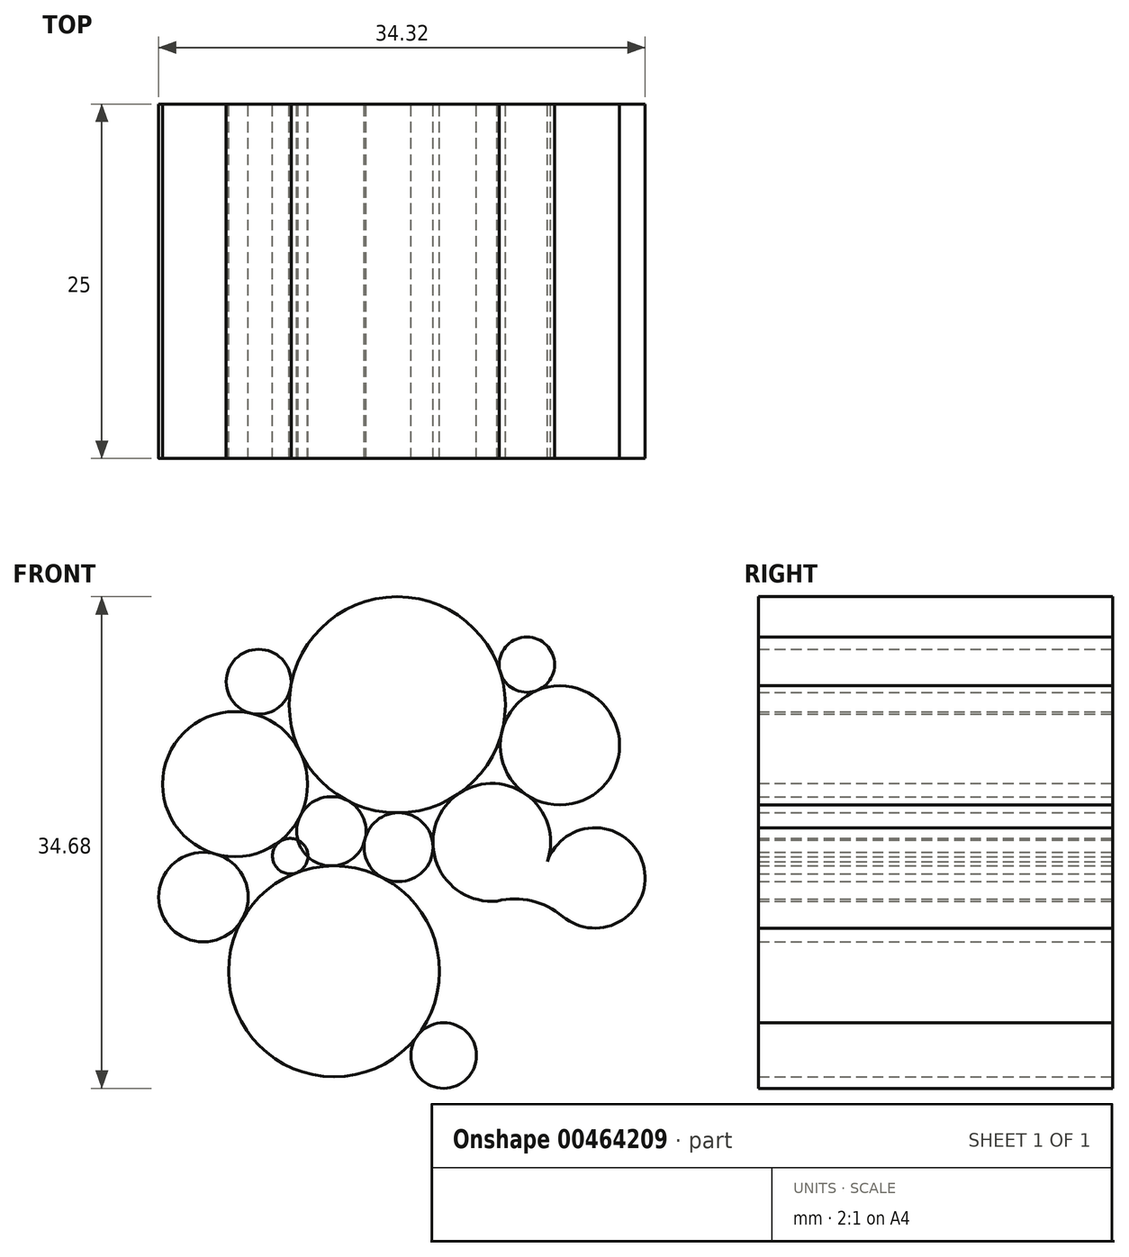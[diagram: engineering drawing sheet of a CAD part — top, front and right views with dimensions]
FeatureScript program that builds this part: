
annotation { "Feature Type Name" : "Feature", "Feature Type Description" : "" }
export const myFeature = defineFeature(function(context is Context, id is Id, definition is map)
    precondition{}
    {
        {
            var Q0;
            Q0=qCreatedBy(makeId("Front.planeOp"),FACE);
            var sketch = newSketch(context, id + "F0", { "sketchPlane" : qUnion([Q0])});
            skCircle(sketch, "E0", {"center": v(-5.15, 5.5) * mm, "radius": 17.5 * mm});
            skCircle(sketch, "E1", {"center": v(-5.33, 15.38) * mm, "radius": 7.62 * mm});
            skPoint(sketch, "E1.first.point", {"position": v(-5.47, 23) * mm});
            skPoint(sketch, "E1.second.point", {"position": v(-5.47, 23) * mm});
            skPoint(sketch, "E1.third.point", {"position": v(-3.02, 8.12) * mm});
            skCircle(sketch, "E2", {"center": v(6.14, 12.5) * mm, "radius": 4.2 * mm});
            skPoint(sketch, "E2.first.point", {"position": v(2.06, 13.53) * mm});
            skPoint(sketch, "E2.second.point", {"position": v(9.72, 14.73) * mm});
            skPoint(sketch, "E2.third.point", {"position": v(9.54, 10.03) * mm});
            skCircle(sketch, "E3", {"center": v(-16.77, 9.78) * mm, "radius": 5.12 * mm});
            skPoint(sketch, "E3.first.point", {"position": v(-12.18, 12.03) * mm});
            skPoint(sketch, "E3.second.point", {"position": v(-21.57, 11.55) * mm});
            skPoint(sketch, "E3.third.point", {"position": v(-16.32, 4.68) * mm});
            skCircle(sketch, "E4", {"center": v(3.81, 18.2) * mm, "radius": 1.95 * mm});
            skPoint(sketch, "E4.first.point", {"position": v(1.95, 17.63) * mm});
            skPoint(sketch, "E4.second.point", {"position": v(4.94, 19.8) * mm});
            skPoint(sketch, "E4.third.point", {"position": v(4.55, 16.4) * mm});
            skCircle(sketch, "E5", {"center": v(-9.98, 6.45) * mm, "radius": 2.44 * mm});
            skPoint(sketch, "E5.first.point", {"position": v(-12.18, 7.53) * mm});
            skPoint(sketch, "E5.second.point", {"position": v(-8.85, 8.62) * mm});
            skPoint(sketch, "E5.third.point", {"position": v(-8.97, 4.23) * mm});
            skCircle(sketch, "E6", {"center": v(1.34, 5.67) * mm, "radius": 4.16 * mm});
            skPoint(sketch, "E6.first.point", {"position": v(-1.02, 9.1) * mm});
            skPoint(sketch, "E6.second.point", {"position": v(4.58, 8.27) * mm});
            skPoint(sketch, "E6.third.point", {"position": v(-1.42, 2.56) * mm});
            skCircle(sketch, "E7", {"center": v(-15.1, 17) * mm, "radius": 2.3 * mm});
            skPoint(sketch, "E7.first.point", {"position": v(-16.6, 18.73) * mm});
            skPoint(sketch, "E7.second.point", {"position": v(-15.62, 14.77) * mm});
            skPoint(sketch, "E7.third.point", {"position": v(-12.85, 16.62) * mm});
            skLineSegment(sketch, "E8", {"start": v(3.81, 18.2) * mm, "end": v(1.95, 17.63) * mm, "construction": true});
            skCircle(sketch, "E9", {"center": v(-5.24, 5.33) * mm, "radius": 2.43 * mm});
            skPoint(sketch, "E9.first.point", {"position": v(-7.6, 5.89) * mm});
            skPoint(sketch, "E9.second.point", {"position": v(-5.26, 7.76) * mm});
            skPoint(sketch, "E9.third.point", {"position": v(-3.8, 3.37) * mm});
            skCircle(sketch, "E10", {"center": v(2.94, -3.62) * mm, "radius": 5.3 * mm});
            skPoint(sketch, "E10.first.point", {"position": v(1.71, 1.53) * mm});
            skPoint(sketch, "E10.second.point", {"position": v(-0.07, -7.99) * mm});
            skPoint(sketch, "E10.third.point", {"position": v(2.61, -8.91) * mm});
            skCircle(sketch, "E11", {"center": v(-19, 1.8) * mm, "radius": 3.16 * mm, "construction": true});
            skPoint(sketch, "E11.first.point", {"position": v(-16.28, 0.22) * mm});
            skPoint(sketch, "E11.second.point", {"position": v(-18.15, 4.85) * mm});
            skPoint(sketch, "E11.third.point", {"position": v(-22.06, 1) * mm});
            skCircle(sketch, "E12", {"center": v(-9.8, -3.43) * mm, "radius": 7.44 * mm});
            skPoint(sketch, "E12.first.point", {"position": v(-13.22, -10.03) * mm});
            skPoint(sketch, "E12.second.point", {"position": v(-9.94, 4.01) * mm});
            skPoint(sketch, "E12.third.point", {"position": v(-3.22, -6.9) * mm});
            skPoint(sketch, "E13.first.point", {"position": v(10.78, -1.74) * mm});
            skPoint(sketch, "E13.second.point", {"position": v(9.3, -1.63) * mm});
            skPoint(sketch, "E13.third.point", {"position": v(3.9, -4.41) * mm});
            skPoint(sketch, "E14.first.point", {"position": v(-3.5, -7.39) * mm});
            skPoint(sketch, "E14.third.point", {"position": v(-1.17, -6.97) * mm});
            skCircle(sketch, "E15", {"center": v(-19, 1.8) * mm, "radius": 3.16 * mm});
            skPoint(sketch, "E15.second.point", {"position": v(-15.89, 1.32) * mm});
            skPoint(sketch, "E15.third.point", {"position": v(-21.57, -0.04) * mm});
            skCircle(sketch, "E16", {"center": v(-12.88, 4.7) * mm, "radius": 1.25 * mm});
            skPoint(sketch, "E16.first.point", {"position": v(-13.53, 5.77) * mm});
            skPoint(sketch, "E16.second.point", {"position": v(-12.44, 3.53) * mm});
            skPoint(sketch, "E16.third.point", {"position": v(-11.74, 5.2) * mm});
            skCircle(sketch, "E17", {"center": v(8.61, 3.16) * mm, "radius": 3.54 * mm});
            skPoint(sketch, "E17.first.point", {"position": v(5.3, 1.9) * mm});
            skPoint(sketch, "E17.second.point", {"position": v(9.4, 6.61) * mm});
            skPoint(sketch, "E17.third.point", {"position": v(11.4, 5.33) * mm});
            skPoint(sketch, "E18.first.point", {"position": v(8.43, 5.29) * mm});
            skPoint(sketch, "E18.second.point", {"position": v(2.65, 1) * mm});
            skPoint(sketch, "E18.third.point", {"position": v(10.5, 1) * mm});
            skPoint(sketch, "E19.first.point", {"position": v(-0.71, -8.32) * mm});
            skPoint(sketch, "E19.second.point", {"position": v(3.23, -11.3) * mm});
            skPoint(sketch, "E19.third.point", {"position": v(-5.91, -11.98) * mm});
            skCircle(sketch, "E20", {"center": v(-2.06, -9.37) * mm, "radius": 2.31 * mm});
            skPoint(sketch, "E20.first.point", {"position": v(-4.3, -8.78) * mm});
            skPoint(sketch, "E20.second.point", {"position": v(0.07, -10.29) * mm});
            skPoint(sketch, "E20.third.point", {"position": v(-0.35, -10.93) * mm});
            skPoint(sketch, "E21.first.point", {"position": v(-0.43, -5.07) * mm});
            skPoint(sketch, "E21.second.point", {"position": v(3.23, -5.71) * mm});
            skPoint(sketch, "E22.first.point", {"position": v(15.25, 1.23) * mm});
            skPoint(sketch, "E22.second.point", {"position": v(11.56, -2.12) * mm});
            skPoint(sketch, "E22.third.point", {"position": v(14.07, 1.78) * mm});
            skPoint(sketch, "E23.first.point", {"position": v(12.05, 8.7) * mm});
            skPoint(sketch, "E23.second.point", {"position": v(13.38, 1.8) * mm});
            skPoint(sketch, "E23.third.point", {"position": v(13.66, 9.75) * mm});
            skPoint(sketch, "E24.first.point", {"position": v(12.35, 5.37) * mm});
            skPoint(sketch, "E24.second.point", {"position": v(6.5, 2.96) * mm});
            skPoint(sketch, "E24.third.point", {"position": v(9.59, 2.03) * mm});
            skPoint(sketch, "E25.first.point", {"position": v(-1.15, -7.24) * mm});
            skPoint(sketch, "E25.third.point", {"position": v(4.2, -6.52) * mm});
            skSolve(sketch);
        }
        {
            var Q0;
            {var subQ0=sQuery(id+"F0.wireOp",EDGE,"E4");var subQ1=makeQuery(id+"F0.imprint","INTERSECT",VERTEX,{"derivedFrom":[sQuery(id+"F0.wireOp",EDGE,"E0"),subQ0]});Q0=makeQuery(id+"F0.imprint","IMPRINT",FACE,{"disambiguationData":[TD([[makeQuery(id+"F0.imprint","IMPRINT",EDGE,{"disambiguationData":[TD([[subQ1,-1.0]])],"derivedFrom":subQ0}),1.0]])]});}
            var Q1;
            {var subQ0=sQuery(id+"F0.wireOp",EDGE,"E7");var subQ1=makeQuery(id+"F0.imprint","INTERSECT",VERTEX,{"derivedFrom":[sQuery(id+"F0.wireOp",EDGE,"E0"),subQ0]});Q1=makeQuery(id+"F0.imprint","IMPRINT",FACE,{"disambiguationData":[TD([[makeQuery(id+"F0.imprint","IMPRINT",EDGE,{"disambiguationData":[TD([[subQ1,-1.0]])],"derivedFrom":subQ0}),1.0]])]});}
            var Q2;
            {var subQ0=sQuery(id+"F0.wireOp",EDGE,"E15");var subQ1=makeQuery(id+"F0.imprint","INTERSECT",VERTEX,{"derivedFrom":[sQuery(id+"F0.wireOp",EDGE,"E0"),subQ0]});Q2=makeQuery(id+"F0.imprint","IMPRINT",FACE,{"disambiguationData":[TD([[makeQuery(id+"F0.imprint","IMPRINT",EDGE,{"disambiguationData":[TD([[subQ1,1.0]])],"derivedFrom":subQ0}),1.0]])]});}
            var Q3;
            {var subQ0=sQuery(id+"F0.wireOp",EDGE,"E17");var subQ1=makeQuery(id+"F0.imprint","INTERSECT",VERTEX,{"derivedFrom":[sQuery(id+"F0.wireOp",EDGE,"E6"),subQ0]});Q3=makeQuery(id+"F0.imprint","IMPRINT",FACE,{"disambiguationData":[TD([[makeQuery(id+"F0.imprint","IMPRINT",EDGE,{"disambiguationData":[TD([[subQ1,-1.0]])],"derivedFrom":subQ0}),1.0]])]});}
            var Q4;
            {var subQ0=sQuery(id+"F0.wireOp",EDGE,"E20");var subQ1=makeQuery(id+"F0.imprint","INTERSECT",VERTEX,{"derivedFrom":[sQuery(id+"F0.wireOp",EDGE,"E10"),subQ0]});Q4=makeQuery(id+"F0.imprint","IMPRINT",FACE,{"disambiguationData":[TD([[makeQuery(id+"F0.imprint","IMPRINT",EDGE,{"disambiguationData":[TD([[subQ1,-1.0]])],"derivedFrom":subQ0}),1.0]])]});}
            var Q5;
            {var subQ0=sQuery(id+"F0.wireOp",EDGE,"E2");var subQ1=makeQuery(id+"F0.imprint","INTERSECT",VERTEX,{"derivedFrom":[sQuery(id+"F0.wireOp",EDGE,"E0"),subQ0]});Q5=makeQuery(id+"F0.imprint","IMPRINT",FACE,{"disambiguationData":[TD([[makeQuery(id+"F0.imprint","IMPRINT",EDGE,{"disambiguationData":[TD([[subQ1,-1.0]])],"derivedFrom":subQ0}),1.0]])]});}
            var Q6;
            {var subQ0=sQuery(id+"F0.wireOp",EDGE,"E3");var subQ5=makeQuery(id+"F0.imprint","INTERSECT",VERTEX,{"derivedFrom":[sQuery(id+"F0.wireOp",EDGE,"E1"),subQ0]});Q6=makeQuery(id+"F0.imprint","IMPRINT",FACE,{"disambiguationData":[TD([[makeQuery(id+"F0.imprint","IMPRINT",EDGE,{"disambiguationData":[TD([[subQ5,-1.0]])],"derivedFrom":subQ0}),1.0]])]});}
            var Q7;
            {var subQ0=sQuery(id+"F0.wireOp",EDGE,"E10");var subQ3=sQuery(id+"F0.wireOp",EDGE,"E6");var subQ4=makeQuery(id+"F0.imprint","INTERSECT",VERTEX,{"disambiguationData":[OD(0.0)],"derivedFrom":[subQ3,subQ0]});Q7=makeQuery(id+"F0.imprint","IMPRINT",FACE,{"disambiguationData":[TD([[makeQuery(id+"F0.imprint","IMPRINT",EDGE,{"disambiguationData":[TD([[subQ4,-1.0]])],"derivedFrom":subQ3}),-1.0]])]});}
            var Q8;
            {var subQ0=sQuery(id+"F0.wireOp",EDGE,"E12");var subQ4=makeQuery(id+"F0.imprint","INTERSECT",VERTEX,{"derivedFrom":[sQuery(id+"F0.wireOp",EDGE,"E9"),subQ0]});Q8=makeQuery(id+"F0.imprint","IMPRINT",FACE,{"disambiguationData":[TD([[makeQuery(id+"F0.imprint","IMPRINT",EDGE,{"disambiguationData":[TD([[subQ4,1.0]])],"derivedFrom":subQ0}),1.0]])]});}
            var Q9;
            {var subQ0=sQuery(id+"F0.wireOp",EDGE,"E1");var subQ4=makeQuery(id+"F0.imprint","INTERSECT",VERTEX,{"derivedFrom":[sQuery(id+"F0.wireOp",EDGE,"E0"),subQ0]});Q9=makeQuery(id+"F0.imprint","IMPRINT",FACE,{"disambiguationData":[TD([[makeQuery(id+"F0.imprint","IMPRINT",EDGE,{"disambiguationData":[TD([[subQ4,1.0]])],"derivedFrom":subQ0}),1.0]])]});}
            var Q10;
            {var subQ0=sQuery(id+"F0.wireOp",EDGE,"E5");var subQ7=makeQuery(id+"F0.imprint","INTERSECT",VERTEX,{"derivedFrom":[sQuery(id+"F0.wireOp",EDGE,"E1"),subQ0]});Q10=makeQuery(id+"F0.imprint","IMPRINT",FACE,{"disambiguationData":[TD([[makeQuery(id+"F0.imprint","IMPRINT",EDGE,{"disambiguationData":[TD([[subQ7,-1.0]])],"derivedFrom":subQ0}),1.0]])]});}
            var Q11;
            {var subQ0=sQuery(id+"F0.wireOp",EDGE,"E16");var subQ1=sQuery(id+"F0.wireOp",EDGE,"E5");var subQ2=makeQuery(id+"F0.imprint","INTERSECT",VERTEX,{"disambiguationData":[OD(0.0)],"derivedFrom":[subQ1,subQ0]});Q11=makeQuery(id+"F0.imprint","IMPRINT",FACE,{"disambiguationData":[TD([[makeQuery(id+"F0.imprint","IMPRINT",EDGE,{"disambiguationData":[TD([[subQ2,-1.0]])],"derivedFrom":subQ1}),-1.0]])]});}
            var Q12;
            {var subQ0=sQuery(id+"F0.wireOp",EDGE,"E9");var subQ1=makeQuery(id+"F0.imprint","INTERSECT",VERTEX,{"derivedFrom":[sQuery(id+"F0.wireOp",EDGE,"E1"),subQ0]});Q12=makeQuery(id+"F0.imprint","IMPRINT",FACE,{"disambiguationData":[TD([[makeQuery(id+"F0.imprint","IMPRINT",EDGE,{"disambiguationData":[TD([[subQ1,1.0]])],"derivedFrom":subQ0}),1.0]])]});}
            var Q13;
            {var subQ1=sQuery(id+"F0.wireOp",EDGE,"E6");var subQ6=makeQuery(id+"F0.imprint","INTERSECT",VERTEX,{"derivedFrom":[sQuery(id+"F0.wireOp",EDGE,"E1"),subQ1]});Q13=makeQuery(id+"F0.imprint","IMPRINT",FACE,{"disambiguationData":[TD([[makeQuery(id+"F0.imprint","IMPRINT",EDGE,{"disambiguationData":[TD([[subQ6,1.0]])],"derivedFrom":subQ1}),1.0]])]});}
            extrude(context, id + "F1", {"entities" : qUnion([Q0, Q1, Q2, Q3, Q4, Q5, Q6, Q7, Q8, Q9, Q10, Q11, Q12, Q13]), "depth" : 25 * mm});
        }
    });
